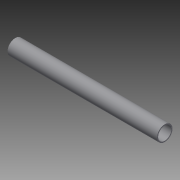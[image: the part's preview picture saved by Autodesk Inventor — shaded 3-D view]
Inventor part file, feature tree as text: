
AUTODESK INVENTOR PART (.ipt)
format: ipt  version: 2015 SP1 (Build 190203100, 203)  size: 72,192 bytes
history: native  units: in
note: dims shown in document units (in); Inventor stores cm internally (conversion verified against a paired STEP export)
features: extrude x1, sketch x1
ambient origin geometry x8: Origin, YZ Plane, XZ Plane, XY Plane, X Axis, Y Axis, Z Axis, Center Point
bodies: Solid1 (feature_tree)
feature tree (2):
  extrude  "Extrusion1"  Depth=23.0in
  sketch  "Sketch1"  dims[d0=2.047in d1=2.375in d2=23.0in d3=0.0in]
